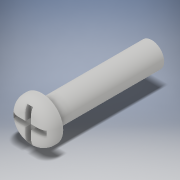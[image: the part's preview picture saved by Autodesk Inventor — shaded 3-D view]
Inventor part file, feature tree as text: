
AUTODESK INVENTOR PART (.ipt)
format: ipt  version: 2018 (Build 220112000, 112)  size: 146,944 bytes
history: native  units: in
note: dims shown in document units (in); Inventor stores cm internally (conversion verified against a paired STEP export)
features: extrude x3, sketch x3, fillet x1
ambient origin geometry x8: Origin, YZ Plane, XZ Plane, XY Plane, X Axis, Y Axis, Z Axis, Center Point
bodies: Solid1 (feature_tree)
feature tree (7):
  extrude  "Extrusion1"  Depth=0.0984in TaperAngle=0.0deg
  extrude  "Extrusion2"  Depth=0.7874in TaperAngle=0.0deg
  fillet  "Fillet1"  Radius=0.0787in
  extrude  "Extrusion3"  Depth=0.0394in
  sketch  "Sketch1"  dims[d0=0.3051in d1=0.0984in d2=0.0in]
  sketch  "Sketch2"  dims[d3=0.1772in d4=0.7874in d5=0.0in d6=0.0787in]
  sketch  "Sketch3"  dims[d7=0.0394in d8=0.0394in d9=0.2362in d10=0.2362in d11=0.0394in d12=0.0in]
